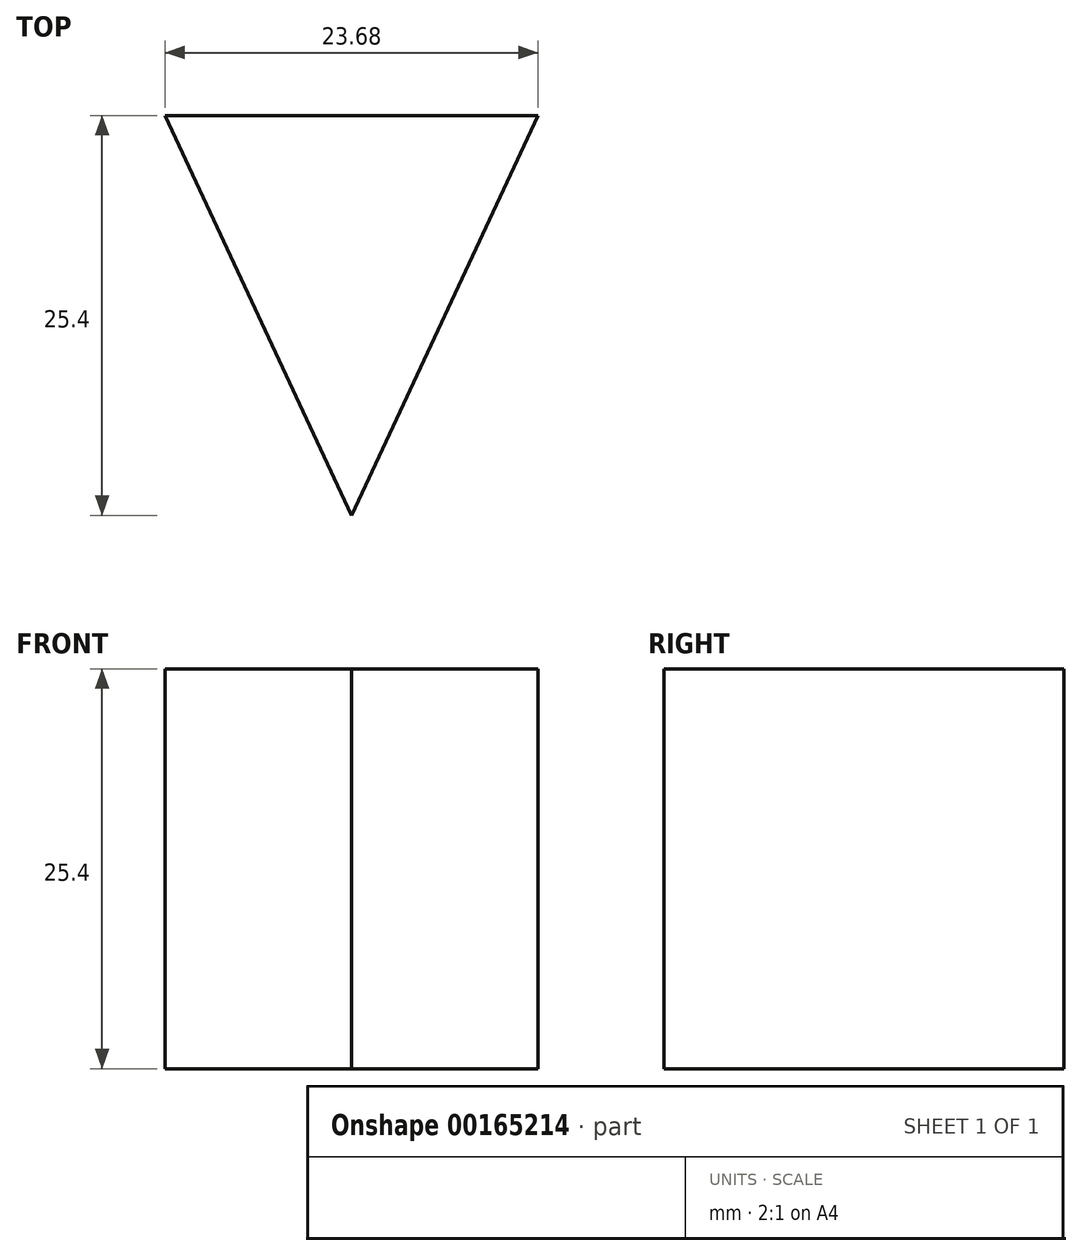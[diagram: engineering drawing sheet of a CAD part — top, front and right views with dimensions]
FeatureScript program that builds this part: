
annotation { "Feature Type Name" : "Feature", "Feature Type Description" : "" }
export const myFeature = defineFeature(function(context is Context, id is Id, definition is map)
    precondition{}
    {
        {
            var Q0;
            Q0=qCreatedBy(makeId("Top.planeOp"),FACE);
            var sketch = newSketch(context, id + "F0", { "sketchPlane" : qUnion([Q0])});
            skLineSegment(sketch, "E0", {"start": v(0, 0) * mm, "end": v(11.84, 25.4) * mm});
            skLineSegment(sketch, "E1", {"start": v(11.84, 25.4) * mm, "end": v(-11.84, 25.4) * mm});
            skLineSegment(sketch, "E2", {"start": v(-11.84, 25.4) * mm, "end": v(0, 0) * mm});
            skLineSegment(sketch, "E3", {"start": v(0, 25.4) * mm, "end": v(0, 0) * mm, "construction": true});
            skSolve(sketch);
        }
        {
            var Q0;
            Q0 = qSketchRegion(id + "F0", true);
            extrude(context, id + "F1", {"entities" : qUnion([Q0]), "depth" : 25.4 * mm});
        }
    });
